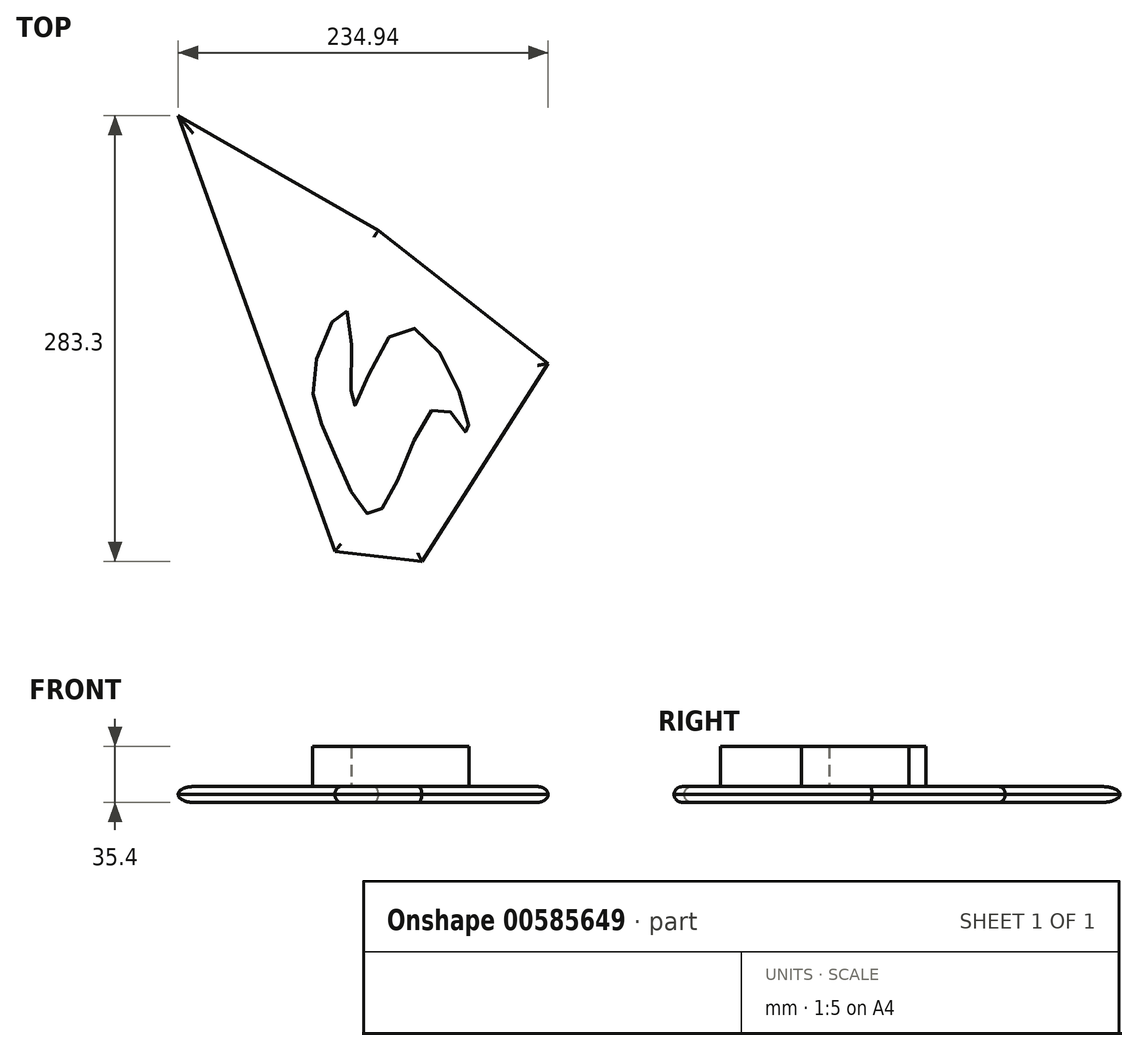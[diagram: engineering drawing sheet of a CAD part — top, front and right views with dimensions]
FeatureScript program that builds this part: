
annotation { "Feature Type Name" : "Feature", "Feature Type Description" : "" }
export const myFeature = defineFeature(function(context is Context, id is Id, definition is map)
    precondition{}
    {
        {
            var Q0;
            Q0=qCreatedBy(makeId("Top.planeOp"),FACE);
            var sketch = newSketch(context, id + "F0", { "sketchPlane" : qUnion([Q0])});
            skLineSegment(sketch, "E0", {"start": v(-11.37, 111.88) * mm, "end": v(96.36, 27.25) * mm});
            skLineSegment(sketch, "E1", {"start": v(96.36, 27.25) * mm, "end": v(16.24, -98.52) * mm});
            skLineSegment(sketch, "E2", {"start": v(16.24, -98.52) * mm, "end": v(-38.98, -92.03) * mm});
            skLineSegment(sketch, "E3", {"start": v(-38.98, -92.03) * mm, "end": v(-138.58, 184.78) * mm});
            skLineSegment(sketch, "E4", {"start": v(-138.58, 184.78) * mm, "end": v(-11.37, 111.88) * mm});
            skSolve(sketch);
        }
        {
            var Q0;
            Q0=makeQuery(id+"F0.imprint","IMPRINT",FACE,{"disambiguationData":[TD([[makeQuery(id+"F0.imprint","IMPRINT",EDGE,{"derivedFrom":sQuery(id+"F0.wireOp",EDGE,"E0")}),-1.0]])]});
            extrude(context, id + "F1", {"entities" : qUnion([Q0]), "depth" : 10 * mm, "offsetDistance" : 25.4 * mm});
        }
        {
            var Q0;
            Q0=makeQuery(id+"F1.opExtrude","CAP_FACE",FACE,{"disambiguationData":[OSD([sQuery(id+"F0.wireOp",EDGE,"E0"),sQuery(id+"F0.wireOp",EDGE,"E1"),sQuery(id+"F0.wireOp",EDGE,"E2"),sQuery(id+"F0.wireOp",EDGE,"E3"),sQuery(id+"F0.wireOp",EDGE,"E4")])],"isStart":false});
            var Q1;
            Q1=makeQuery(id+"F1.opExtrude","CAP_EDGE",EDGE,{"disambiguationData":[OSD([sQuery(id+"F0.wireOp",EDGE,"E3")])],"isStart":false});
            fillet(context, id + "F2", {"entities" : qUnion([Q0, Q1]), "radius" : 5.08 * mm, "tangentPropagation" : true, "allowEdgeOverflow" : false});
        }
        {
            var Q0;
            Q0=makeQuery(id+"F1.opExtrude","CAP_FACE",FACE,{"disambiguationData":[OSD([sQuery(id+"F0.wireOp",EDGE,"E0"),sQuery(id+"F0.wireOp",EDGE,"E1"),sQuery(id+"F0.wireOp",EDGE,"E2"),sQuery(id+"F0.wireOp",EDGE,"E3"),sQuery(id+"F0.wireOp",EDGE,"E4")])],"isStart":true});
            fillet(context, id + "F3", {"entities" : qUnion([Q0]), "radius" : 5.08 * mm, "tangentPropagation" : true, "allowEdgeOverflow" : false});
        }
        {
            var Q0;
            Q0=makeQuery(id+"F1.opExtrude","CAP_FACE",FACE,{"disambiguationData":[OSD([sQuery(id+"F0.wireOp",EDGE,"E0"),sQuery(id+"F0.wireOp",EDGE,"E1"),sQuery(id+"F0.wireOp",EDGE,"E2"),sQuery(id+"F0.wireOp",EDGE,"E3"),sQuery(id+"F0.wireOp",EDGE,"E4")])],"isStart":false});
            var sketch = newSketch(context, id + "F4", { "sketchPlane" : qUnion([Q0])});
            skFitSpline(sketch, "E5", {"points": [v(-31.26, 60.58) * mm, v(-52.03, 24.27) * mm, v(-41.23, -25.63) * mm, v(-17.18, -68.56) * mm, v(0, -48.35) * mm, v(28.78, 0) * mm, v(45.15, -17.36) * mm, v(36.87, 17.07) * mm, v(0, 48.52) * mm, v(-27.71, 0) * mm, v(-31.26, 60.58) * mm]});
            skSolve(sketch);
        }
        {
            var Q0;
            Q0=makeQuery(id+"F4.imprint","IMPRINT",FACE,{"disambiguationData":[TD([[makeQuery(id+"F4.imprint","IMPRINT",EDGE,{"derivedFrom":sQuery(id+"F4.wireOp",EDGE,"E5")}),1.0]])]});
            extrude(context, id + "F5", {"entities" : qUnion([Q0]), "operationType" : NewBodyOperationType.ADD, "depth" : 25.4 * mm, "offsetDistance" : 25.4 * mm});
        }
    });
